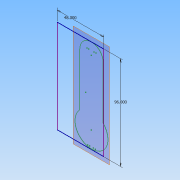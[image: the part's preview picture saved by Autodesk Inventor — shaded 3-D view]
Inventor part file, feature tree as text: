
AUTODESK INVENTOR PART (.ipt)
format: ipt  version: 2013 (Build 170138000, 138)  size: 84,480 bytes
history: native  units: in
note: dims shown in document units (in); Inventor stores cm internally (conversion verified against a paired STEP export)
features: plane x1, extrude x1, sketch x1, reference x1
ambient origin geometry x8: Origin, YZ Plane, XZ Plane, XY Plane, X Axis, Y Axis, Z Axis, Center Point
bodies: Solid1 (feature_tree)
feature tree (4):
  plane  "Work Plane1"
  extrude  "Extrusion1"  Depth=96.0in
  sketch  "Sketch1"  dims[d0=48.0in d2=96.0in d3=0.75in d4=0.0in]
  reference  "Reference1"
